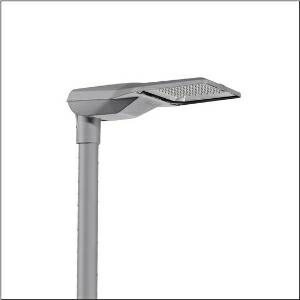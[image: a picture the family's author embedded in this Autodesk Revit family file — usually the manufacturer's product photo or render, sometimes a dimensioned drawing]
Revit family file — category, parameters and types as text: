
# Revit family: streetlight_sl_21_iq_midi___st1_0a_5xe3d21g08nb_5ac0
name_source: partatom
category: Lighting Fixtures
units: mm (PartAtom-declared; Revit-internal decimal feet)

## family parameters
Cut with Voids When Loaded = No
Host = Face
Light Source = No
Part Type = Normal
Room Calculation Point = No
Round Connector Dimension = Use Diameter
Shared = No

## types (1)
- --- (1 x LED, 19210 lm, 155.5 W, 2200K)
    Apparent Load = 155 VA
    CIE Flux Codes = 40 73 97 100 100
    Color Rendering = 70
    Color Temperature = 2200K
    Default Elevation = 1800 mm
    Description = Streetlight SL 21 iQ midi, mast luminaire, primary light control with lens, of PMMA, primary optical cover: cover, of toughened safety glass, transparent, light distribution: ST1.0a, light emission: direct distribution, primary light characteristic: asymmetric, installation type: post-top, side-entry, LED, High Power LED, rated luminous flux: 19.210lm, luminous efficacy: 124lm/W, light colour: 722, colour temperature: 2200K, control gear: iQ Street-Remote, control: Street-Remote, Auto-Match, Temp-Guard, Lumen-Switch, Night-Set, Smart-Wire, Light-Fading, Desk-Remote (wireless, voltage-free reading and setting of iQ features in the workshop via application-optimized NFC function/RFID function), optimised constant luminous flux control (CLO 2.0), pre-setting: linear dimming characteristic, mains connection: 230..240V, AC, 50/60Hz, start of lifetime: 156W, end of service life: 162W, reduction: 69W, luminaire housing, of diecast aluminium, powder-coated, SITECO metallic grey (DB 702S), corrosivity category C5 high according to DIN EN ISO 12944, please order mast flange separately, inclination adjustable: 0°, 5°, 10°, 15°, sealing non-destructively replaceable, multi-level sealing system, length: 644mm, width: 335mm, height: 110mm, mast flange for spigot size: 42mm (side-entry): 5XC10008XM4, 60/48mm (side-entry/post-top): 5XC10108XM2, 76/60mm (side-entry/post-top): 5XC10108XM1, mounting height: 4..8m, protection rating (complete): IP66, insulation class (complete): insulation class II (safety insulation), certification: CE, ENEC, ENEC+, VDE, impact resistance: IK10, permissible operating ambient temperature for outdoor applications: -40..+50°C, standard-compliant lighting for roads and squares, packaging unit: 1 piece

Light Distribution: ST1.0a
    Height = 111 mm
    Lamp = 1 x LED
    Lamp Light Flux = 19210 lm
    Lamp Power = 155.5 W
    Lamp count = 1
    Length = 644 mm
    Luminous efficacy = 124 lm/W
    Manufacturer = Siteco
    ModVariant = No
    Model = 5XE3D21G08NB
    Number of Poles = 1
    OnlyDefault = Yes
    Power Factor = 1
    Product Name = Streetlight SL 21 iQ midi | ST1.0a
    Product group = mast luminaire | pylon top
    ProductGroupID = 6100
    Protection Class = Protection class II
    Protection Degree = IP 66
    RLX_Detail_Level = 1
    RLX_Emergency_Light_Flux = 0 lm
    RLX_Emergency_Type = 0
    RLX_Emergency_Type_DB = No
    RlxData = <blob elided: 27189 chars, md5=35513ad0>
    Socket = socket
    Standby Power = 0 W
    System Light Flux = 19210 lm
    System Power = 155 W
    Type Comments = factory setting: luminous flux: 100 % | dim-lin: 254 | 823 mA
    Type Image = l_1004298.jpg
    URL = http://relux.com
    VarID = @adj_170407
    Voltage = 0 V
    Weight = 0.00 kg
    Width = 336 mm

## geometry (parser evidence)
native form markers: Blend x4, Sweep x11
no freeform markers — native parametric forms only
